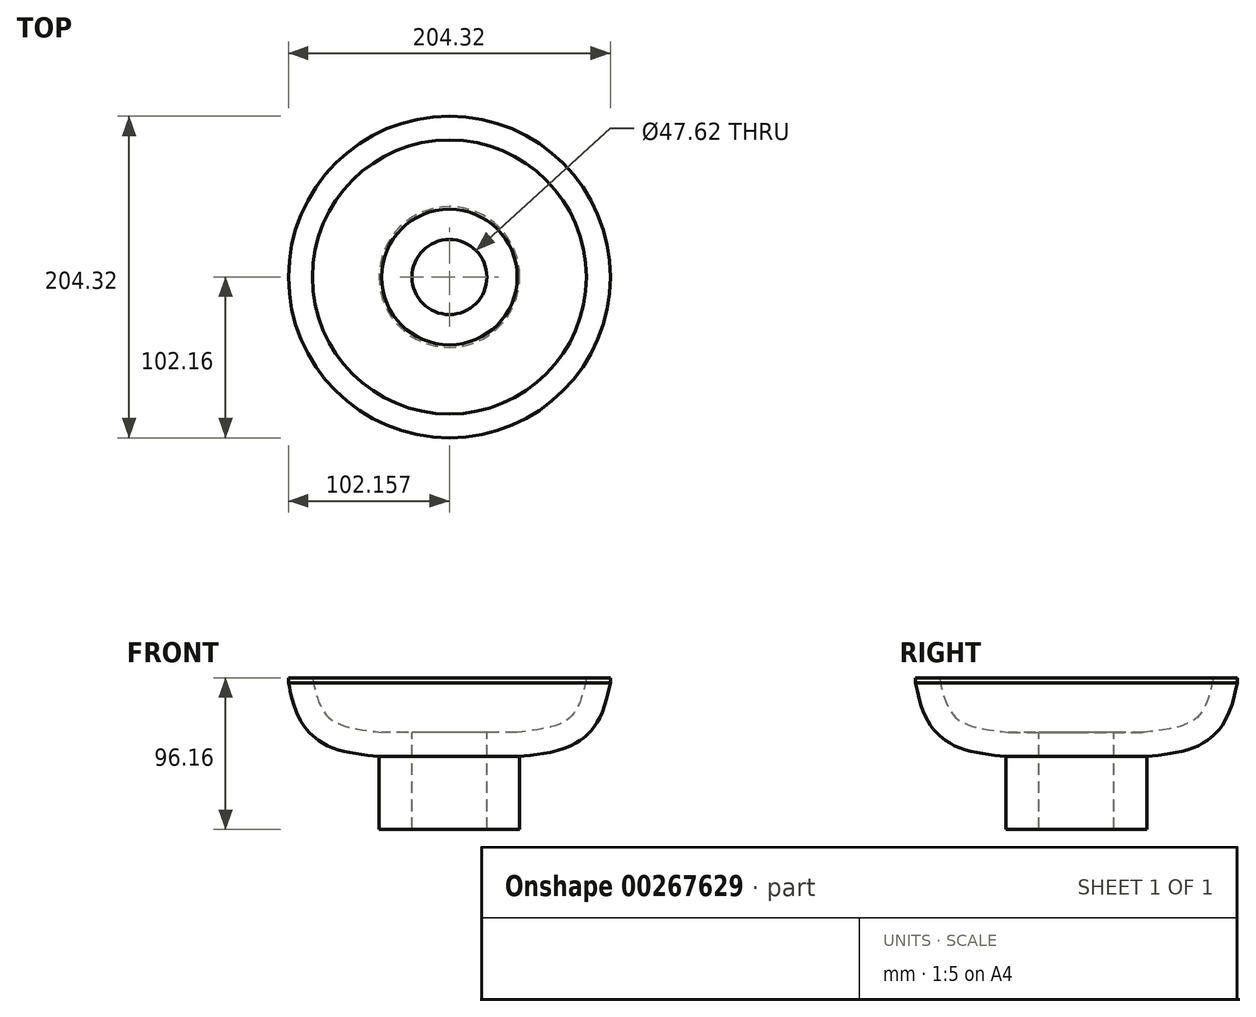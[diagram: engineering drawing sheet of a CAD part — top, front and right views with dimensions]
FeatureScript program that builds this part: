
annotation { "Feature Type Name" : "Feature", "Feature Type Description" : "" }
export const myFeature = defineFeature(function(context is Context, id is Id, definition is map)
    precondition{}
    {
        {
            var Q0;
            Q0=qCreatedBy(makeId("Front.planeOp"),FACE);
            var sketch = newSketch(context, id + "F0", { "sketchPlane" : qUnion([Q0])});
            skFitSpline(sketch, "E0", {"points": [v(43.96, 34.5) * mm, v(33.27, 9.16) * mm, v(0, 0) * mm], "startDerivative": vector(-13.15, -62.3) * mm, "endDerivative": vector(-73.63, -7.72) * mm});
            skFitSpline(sketch, "E1.0", {"points": [v(59.12, 31.3) * mm, v(58.84, 30) * mm, v(58.28, 27.31) * mm, v(57.3, 23.05) * mm, v(56.1, 18.6) * mm, v(54.55, 13.99) * mm, v(52.84, 10.03) * mm, v(51.13, 6.85) * mm, v(49.64, 4.47) * mm, v(47.93, 2.12) * mm, v(46.3, 0.22) * mm, v(44.86, -1.24) * mm, v(43.9, -2.13) * mm, v(43.12, -2.82) * mm, v(42.32, -3.48) * mm, v(41.3, -4.27) * mm, v(40.07, -5.15) * mm, v(38.4, -6.24) * mm, v(35.45, -7.94) * mm, v(31.18, -9.84) * mm, v(26.09, -11.51) * mm, v(21.03, -12.74) * mm, v(16.04, -13.65) * mm, v(11.1, -14.36) * mm, v(6.28, -14.92) * mm, v(3.15, -15.25) * mm, v(1.62, -15.4) * mm]});
            skLineSegment(sketch, "E2", {"start": v(0, 0) * mm, "end": v(-19.23, 0) * mm});
            skLineSegment(sketch, "E3", {"start": v(1.62, -15.4) * mm, "end": v(1.62, -61.66) * mm});
            skLineSegment(sketch, "E4", {"start": v(-19.23, 0) * mm, "end": v(-19.23, -61.66) * mm});
            skLineSegment(sketch, "E5", {"start": v(-19.23, -61.66) * mm, "end": v(1.62, -61.66) * mm});
            skLineSegment(sketch, "E6", {"start": v(59.12, 31.3) * mm, "end": v(59.12, 34.5) * mm});
            skLineSegment(sketch, "E7", {"start": v(59.12, 34.5) * mm, "end": v(43.96, 34.5) * mm});
            skLineSegment(sketch, "E8", {"start": v(-43.04, 34.5) * mm, "end": v(-43.04, -61.66) * mm});
            skPoint(sketch, "E9", {"position": v(51.54, 34.5) * mm});
            skPoint(sketch, "E10", {"position": v(43.28, 31.3) * mm});
            skPoint(sketch, "E11", {"position": v(57.67, 24.7) * mm});
            skSolve(sketch);
        }
        {
            var Q0;
            Q0=makeQuery(id+"F0.imprint","IMPRINT",FACE,{"disambiguationData":[TD([[makeQuery(id+"F0.imprint","IMPRINT",EDGE,{"derivedFrom":sQuery(id+"F0.wireOp",EDGE,"E0")}),1.0]])]});
            var Q1;
            Q1=sQuery(id+"F0.wireOp",EDGE,"E8");
            revolve(context, id + "F1", {"entities" : qUnion([Q0]), "axis" : qUnion([Q1]), "revolveType" : RevolveType.FULL});
        }
    });
